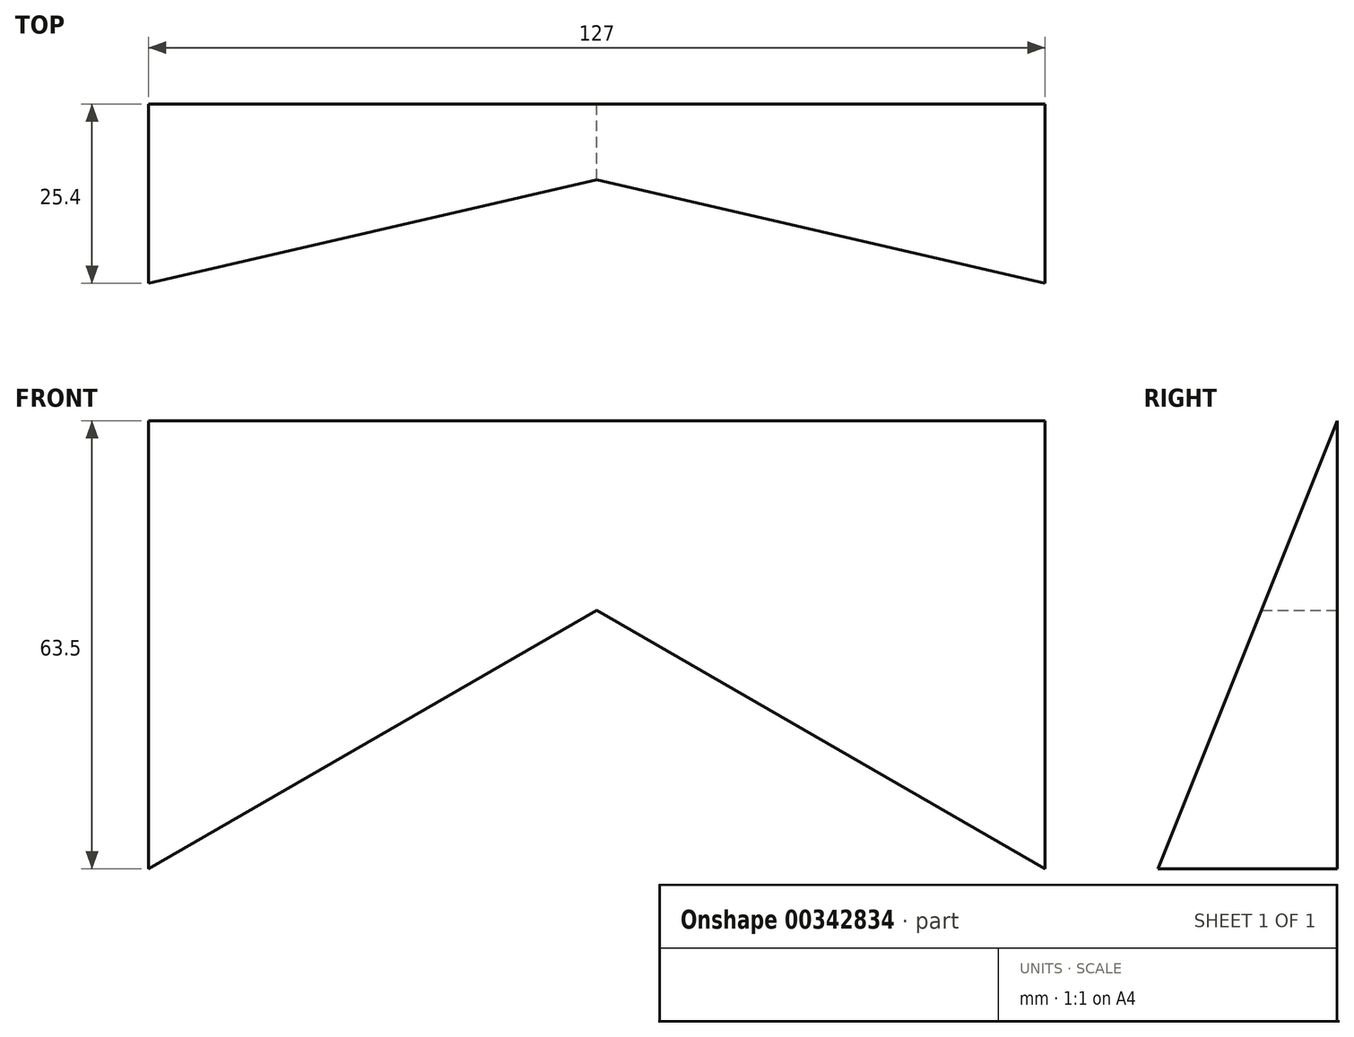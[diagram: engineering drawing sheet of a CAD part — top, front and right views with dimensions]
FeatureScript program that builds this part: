
annotation { "Feature Type Name" : "Feature", "Feature Type Description" : "" }
export const myFeature = defineFeature(function(context is Context, id is Id, definition is map)
    precondition{}
    {
        {
            var Q0;
            Q0=qCreatedBy(makeId("Front.planeOp"),FACE);
            var sketch = newSketch(context, id + "F0", { "sketchPlane" : qUnion([Q0])});
            skLineSegment(sketch, "E0", {"start": v(-40.8, 22.3) * mm, "end": v(86.2, 22.3) * mm});
            skLineSegment(sketch, "E1", {"start": v(86.2, 22.3) * mm, "end": v(86.2, -41.2) * mm});
            skLineSegment(sketch, "E2", {"start": v(-40.8, -41.2) * mm, "end": v(-40.8, 22.3) * mm});
            skLineSegment(sketch, "E3", {"start": v(-40.8, -41.2) * mm, "end": v(22.7, -4.54) * mm});
            skPoint(sketch, "E3.endSnap0", {"position": v(22.7, 22.3) * mm});
            skLineSegment(sketch, "E4", {"start": v(22.7, -4.54) * mm, "end": v(86.2, -41.2) * mm});
            skSolve(sketch);
        }
        {
            var Q0;
            Q0 = qSketchRegion(id + "F0", true);
            extrude(context, id + "F1", {"entities" : qUnion([Q0]), "depth" : 25.4 * mm});
        }
        {
            var Q0;
            Q0=makeQuery(id+"F1.opExtrude","SWEPT_FACE",FACE,{"disambiguationData":[OSD([sQuery(id+"F0.wireOp",EDGE,"E1")])]});
            var sketch = newSketch(context, id + "F2", { "sketchPlane" : qUnion([Q0])});
            skLineSegment(sketch, "E5", {"start": v(-25.4, -41.2) * mm, "end": v(0, 22.3) * mm});
            skLineSegment(sketch, "E6", {"start": v(0, 22.3) * mm, "end": v(-25.4, 22.3) * mm});
            skLineSegment(sketch, "E7", {"start": v(-25.4, 22.3) * mm, "end": v(-25.4, -41.2) * mm});
            skSolve(sketch);
        }
        {
            var Q0;
            Q0 = qSketchRegion(id + "F2", true);
            extrude(context, id + "F3", {"entities" : qUnion([Q0]), "operationType" : NewBodyOperationType.REMOVE, "oppositeDirection" : true, "depth" : 127 * mm});
        }
    });
